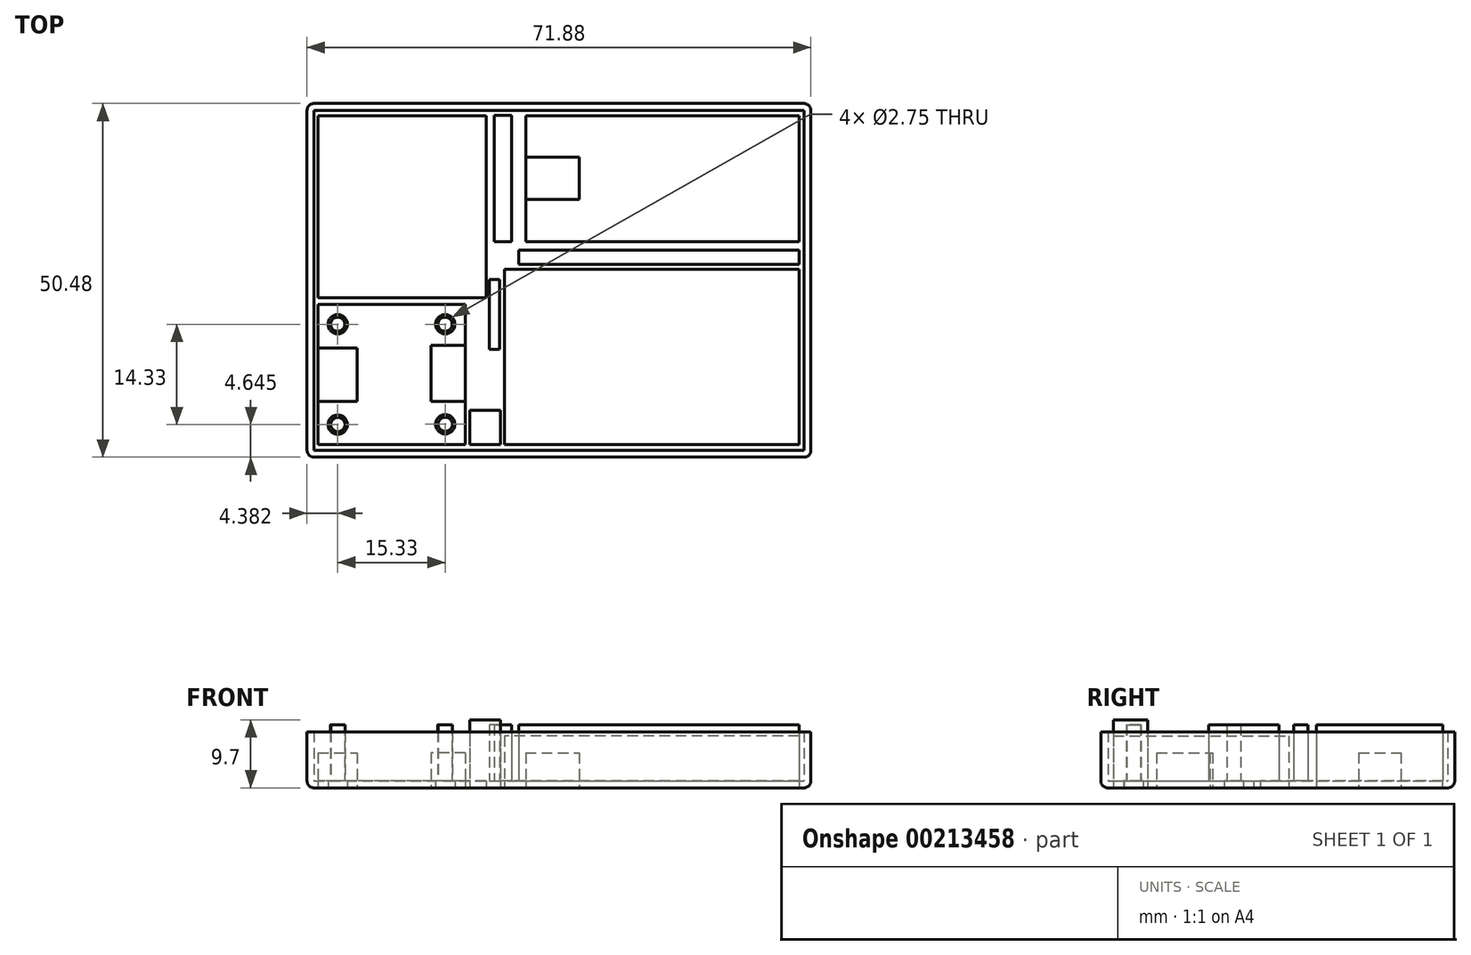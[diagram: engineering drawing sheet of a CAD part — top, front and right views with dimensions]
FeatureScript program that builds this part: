
annotation { "Feature Type Name" : "Feature", "Feature Type Description" : "" }
export const myFeature = defineFeature(function(context is Context, id is Id, definition is map)
    precondition{}
    {
        {
            var Q0;
            Q0=qCreatedBy(makeId("Top.planeOp"),FACE);
            var sketch = newSketch(context, id + "F0", { "sketchPlane" : qUnion([Q0])});
            skLineSegment(sketch, "E0.bottom", {"start": v(0, 0) * mm, "end": v(-42, 0) * mm});
            skLineSegment(sketch, "E0.top", {"start": v(0, 25) * mm, "end": v(-42, 25) * mm});
            skLineSegment(sketch, "E0.left", {"start": v(0, 0) * mm, "end": v(0, 25) * mm});
            skLineSegment(sketch, "E0.right", {"start": v(-42, 0) * mm, "end": v(-42, 25) * mm});
            skLineSegment(sketch, "E1.bottom", {"start": v(0, 28.93) * mm, "end": v(-39, 28.93) * mm});
            skLineSegment(sketch, "E1.top", {"start": v(0, 46.93) * mm, "end": v(-39, 46.93) * mm});
            skLineSegment(sketch, "E1.left", {"start": v(0, 28.93) * mm, "end": v(0, 46.93) * mm});
            skLineSegment(sketch, "E1.right", {"start": v(-39, 28.93) * mm, "end": v(-39, 46.93) * mm});
            skLineSegment(sketch, "E2.bottom", {"start": v(-47.61, 0) * mm, "end": v(-68.61, 0) * mm});
            skLineSegment(sketch, "E2.top", {"start": v(-47.61, 20) * mm, "end": v(-68.61, 20) * mm});
            skLineSegment(sketch, "E2.left", {"start": v(-47.61, 0) * mm, "end": v(-47.61, 20) * mm});
            skLineSegment(sketch, "E2.right", {"start": v(-68.61, 0) * mm, "end": v(-68.61, 20) * mm});
            skLineSegment(sketch, "E3.bottom", {"start": v(-44.64, 46.93) * mm, "end": v(-68.64, 46.93) * mm});
            skLineSegment(sketch, "E3.top", {"start": v(-44.64, 20.93) * mm, "end": v(-68.64, 20.93) * mm});
            skLineSegment(sketch, "E3.left", {"start": v(-44.64, 46.93) * mm, "end": v(-44.64, 20.93) * mm});
            skLineSegment(sketch, "E3.right", {"start": v(-68.64, 46.93) * mm, "end": v(-68.64, 20.93) * mm});
            skLineSegment(sketch, "E4.bottom", {"start": v(-68.61, 13.76) * mm, "end": v(-63.07, 13.76) * mm});
            skLineSegment(sketch, "E4.top", {"start": v(-68.61, 6.14) * mm, "end": v(-63.07, 6.14) * mm});
            skLineSegment(sketch, "E4.left", {"start": v(-68.61, 13.76) * mm, "end": v(-68.61, 6.14) * mm});
            skLineSegment(sketch, "E4.right", {"start": v(-63.07, 13.76) * mm, "end": v(-63.07, 6.14) * mm});
            skLineSegment(sketch, "E5.bottom", {"start": v(-39, 41) * mm, "end": v(-31.35, 41) * mm});
            skLineSegment(sketch, "E5.top", {"start": v(-39, 34.99) * mm, "end": v(-31.35, 34.99) * mm});
            skLineSegment(sketch, "E5.left", {"start": v(-39, 41) * mm, "end": v(-39, 34.99) * mm});
            skLineSegment(sketch, "E5.right", {"start": v(-31.35, 41) * mm, "end": v(-31.35, 34.99) * mm});
            skLineSegment(sketch, "E6.bottom", {"start": v(-47.61, 14.14) * mm, "end": v(-52.5, 14.14) * mm});
            skLineSegment(sketch, "E6.top", {"start": v(-47.61, 6.14) * mm, "end": v(-52.5, 6.14) * mm});
            skLineSegment(sketch, "E6.left", {"start": v(-47.61, 14.14) * mm, "end": v(-47.61, 6.14) * mm});
            skLineSegment(sketch, "E6.right", {"start": v(-52.5, 14.14) * mm, "end": v(-52.5, 6.14) * mm});
            skCircle(sketch, "E7", {"center": v(-65.8, 2.83) * mm, "radius": 1.38 * mm});
            skCircle(sketch, "E8", {"center": v(-50.48, 2.89) * mm, "radius": 1.38 * mm});
            skCircle(sketch, "E9", {"center": v(-65.8, 17.16) * mm, "radius": 1.38 * mm});
            skCircle(sketch, "E10", {"center": v(-50.48, 17.16) * mm, "radius": 1.38 * mm});
            skLineSegment(sketch, "E11.bottom", {"start": v(-46.98, 0) * mm, "end": v(-42.58, 0) * mm});
            skLineSegment(sketch, "E11.top", {"start": v(-46.98, 4.9) * mm, "end": v(-42.58, 4.9) * mm});
            skLineSegment(sketch, "E11.left", {"start": v(-46.98, 0) * mm, "end": v(-46.98, 4.9) * mm});
            skLineSegment(sketch, "E11.right", {"start": v(-42.58, 0) * mm, "end": v(-42.58, 4.9) * mm});
            skSolve(sketch);
        }
        {
            var Q0;
            Q0=makeQuery(id+"F0.imprint","IMPRINT",FACE,{"disambiguationData":[TD([[makeQuery(id+"F0.imprint","IMPRINT",EDGE,{"derivedFrom":sQuery(id+"F0.wireOp",EDGE,"E0.bottom")}),-1.0]])]});
            extrude(context, id + "F1", {"entities" : qUnion([Q0]), "depth" : 7.4 * mm});
        }
        {
            var Q0;
            Q0 = qSketchRegion(id + "F0", true);
            extrude(context, id + "F2", {"entities" : qUnion([Q0]), "depth" : 1 * mm});
        }
        {
            var Q0;
            Q0=makeQuery(id+"F0.imprint","IMPRINT",FACE,{"disambiguationData":[TD([[makeQuery(id+"F0.imprint","IMPRINT",EDGE,{"derivedFrom":sQuery(id+"F0.wireOp",EDGE,"E4.bottom")}),-1.0]])]});
            var Q1;
            Q1=makeQuery(id+"F0.imprint","IMPRINT",FACE,{"disambiguationData":[TD([[makeQuery(id+"F0.imprint","IMPRINT",EDGE,{"derivedFrom":sQuery(id+"F0.wireOp",EDGE,"E6.bottom")}),1.0]])]});
            var Q2;
            Q2=makeQuery(id+"F0.imprint","IMPRINT",FACE,{"disambiguationData":[TD([[makeQuery(id+"F0.imprint","IMPRINT",EDGE,{"derivedFrom":sQuery(id+"F0.wireOp",EDGE,"E5.bottom")}),-1.0]])]});
            extrude(context, id + "F3", {"entities" : qUnion([Q0, Q1, Q2]), "depth" : 5 * mm});
        }
        {
            var Q0;
            Q0=makeQuery(id+"F2.opExtrude","CAP_FACE",FACE,{"disambiguationData":[OSD([sQuery(id+"F0.wireOp",EDGE,"E11.bottom"),sQuery(id+"F0.wireOp",EDGE,"E11.top"),sQuery(id+"F0.wireOp",EDGE,"E11.left"),sQuery(id+"F0.wireOp",EDGE,"E11.right")])],"isStart":false});
            extrude(context, id + "F4", {"entities" : qUnion([Q0]), "operationType" : NewBodyOperationType.ADD, "depth" : 8.7 * mm});
        }
        {
            var Q0;
            Q0=qCreatedBy(makeId("Top.planeOp"),FACE);
            var sketch = newSketch(context, id + "F5", { "sketchPlane" : qUnion([Q0])});
            skLineSegment(sketch, "E12.bottom", {"start": v(-70.19, -1.8) * mm, "end": v(1.7, -1.8) * mm});
            skLineSegment(sketch, "E12.top", {"start": v(-70.19, 48.67) * mm, "end": v(1.7, 48.67) * mm});
            skLineSegment(sketch, "E12.left", {"start": v(-70.19, -1.8) * mm, "end": v(-70.19, 48.67) * mm});
            skLineSegment(sketch, "E12.right", {"start": v(1.7, -1.8) * mm, "end": v(1.7, 48.67) * mm});
            skSolve(sketch);
        }
        {
            var Q0;
            Q0=makeQuery(id+"F5.imprint","IMPRINT",FACE,{"disambiguationData":[TD([[makeQuery(id+"F5.imprint","IMPRINT",EDGE,{"derivedFrom":sQuery(id+"F5.wireOp",EDGE,"E12.bottom")}),1.0]])]});
            extrude(context, id + "F6", {"entities" : qUnion([Q0]), "depth" : 8 * mm});
        }
        {
            var Q0;
            Q0=makeQuery(id+"F6.opExtrude","CAP_FACE",FACE,{"disambiguationData":[OSD([sQuery(id+"F5.wireOp",EDGE,"E12.bottom"),sQuery(id+"F5.wireOp",EDGE,"E12.top"),sQuery(id+"F5.wireOp",EDGE,"E12.left"),sQuery(id+"F5.wireOp",EDGE,"E12.right")])],"isStart":false});
            shell(context, id + "F7", {"entities" : qUnion([Q0]), "thickness" : 1 * mm});
        }
        {
            var Q0;
            Q0=makeQuery(id+"F6.opExtrude","SWEPT_EDGE",EDGE,{"disambiguationData":[OSD([sQuery(id+"F5.wireOp",EDGE,"E12.bottom"),sQuery(id+"F5.wireOp",EDGE,"E12.left")])]});
            var Q1;
            Q1=makeQuery(id+"F6.opExtrude","SWEPT_EDGE",EDGE,{"disambiguationData":[OSD([sQuery(id+"F5.wireOp",EDGE,"E12.bottom"),sQuery(id+"F5.wireOp",EDGE,"E12.right")])]});
            var Q2;
            Q2=makeQuery(id+"F6.opExtrude","SWEPT_EDGE",EDGE,{"disambiguationData":[OSD([sQuery(id+"F5.wireOp",EDGE,"E12.top"),sQuery(id+"F5.wireOp",EDGE,"E12.right")])]});
            var Q3;
            Q3=makeQuery(id+"F6.opExtrude","SWEPT_EDGE",EDGE,{"disambiguationData":[OSD([sQuery(id+"F5.wireOp",EDGE,"E12.top"),sQuery(id+"F5.wireOp",EDGE,"E12.left")])]});
            var Q4;
            Q4=makeQuery(id+"F6.opExtrude","CAP_EDGE",EDGE,{"disambiguationData":[OSD([sQuery(id+"F5.wireOp",EDGE,"E12.bottom")])],"isStart":true});
            var Q5;
            Q5=makeQuery(id+"F6.opExtrude","CAP_EDGE",EDGE,{"disambiguationData":[OSD([sQuery(id+"F5.wireOp",EDGE,"E12.top")])],"isStart":true});
            var Q6;
            Q6=makeQuery(id+"F6.opExtrude","CAP_EDGE",EDGE,{"disambiguationData":[OSD([sQuery(id+"F5.wireOp",EDGE,"E12.right")])],"isStart":true});
            var Q7;
            Q7=makeQuery(id+"F6.opExtrude","CAP_EDGE",EDGE,{"disambiguationData":[OSD([sQuery(id+"F5.wireOp",EDGE,"E12.left")])],"isStart":true});
            fillet(context, id + "F8", {"entities" : qUnion([Q0, Q1, Q2, Q3, Q4, Q5, Q6, Q7]), "radius" : 1 * mm, "tangentPropagation" : true, "allowEdgeOverflow" : false});
        }
        {
            var Q0;
            Q0=qCreatedBy(makeId("Top.planeOp"),FACE);
            var sketch = newSketch(context, id + "F9", { "sketchPlane" : qUnion([Q0])});
            skLineSegment(sketch, "E13.bottom", {"start": v(0, 25.73) * mm, "end": v(-40, 25.73) * mm});
            skLineSegment(sketch, "E13.top", {"start": v(0, 27.73) * mm, "end": v(-40, 27.73) * mm});
            skLineSegment(sketch, "E13.left", {"start": v(0, 25.73) * mm, "end": v(0, 27.73) * mm});
            skLineSegment(sketch, "E13.right", {"start": v(-40, 25.73) * mm, "end": v(-40, 27.73) * mm});
            skLineSegment(sketch, "E14.bottom", {"start": v(-42.7, 23.58) * mm, "end": v(-44.2, 23.58) * mm});
            skLineSegment(sketch, "E14.top", {"start": v(-42.7, 13.58) * mm, "end": v(-44.2, 13.58) * mm});
            skLineSegment(sketch, "E14.left", {"start": v(-42.7, 23.58) * mm, "end": v(-42.7, 13.58) * mm});
            skLineSegment(sketch, "E14.right", {"start": v(-44.2, 23.58) * mm, "end": v(-44.2, 13.58) * mm});
            skLineSegment(sketch, "E15.bottom", {"start": v(-43.49, 46.97) * mm, "end": v(-40.99, 46.97) * mm});
            skLineSegment(sketch, "E15.top", {"start": v(-43.49, 28.97) * mm, "end": v(-40.99, 28.97) * mm});
            skLineSegment(sketch, "E15.left", {"start": v(-43.49, 46.97) * mm, "end": v(-43.49, 28.97) * mm});
            skLineSegment(sketch, "E15.right", {"start": v(-40.99, 46.97) * mm, "end": v(-40.99, 28.97) * mm});
            skCircle(sketch, "E16", {"center": v(-65.82, 17.17) * mm, "radius": 1.01 * mm});
            skCircle(sketch, "E17", {"center": v(-65.79, 2.85) * mm, "radius": 1.01 * mm});
            skCircle(sketch, "E18", {"center": v(-50.46, 2.88) * mm, "radius": 1.01 * mm});
            skCircle(sketch, "E19", {"center": v(-50.5, 17.17) * mm, "radius": 1.01 * mm});
            skSolve(sketch);
        }
        {
            var Q0;
            Q0 = qSketchRegion(id + "F9", true);
            extrude(context, id + "F10", {"entities" : qUnion([Q0]), "operationType" : NewBodyOperationType.ADD, "depth" : 9 * mm});
        }
    });
